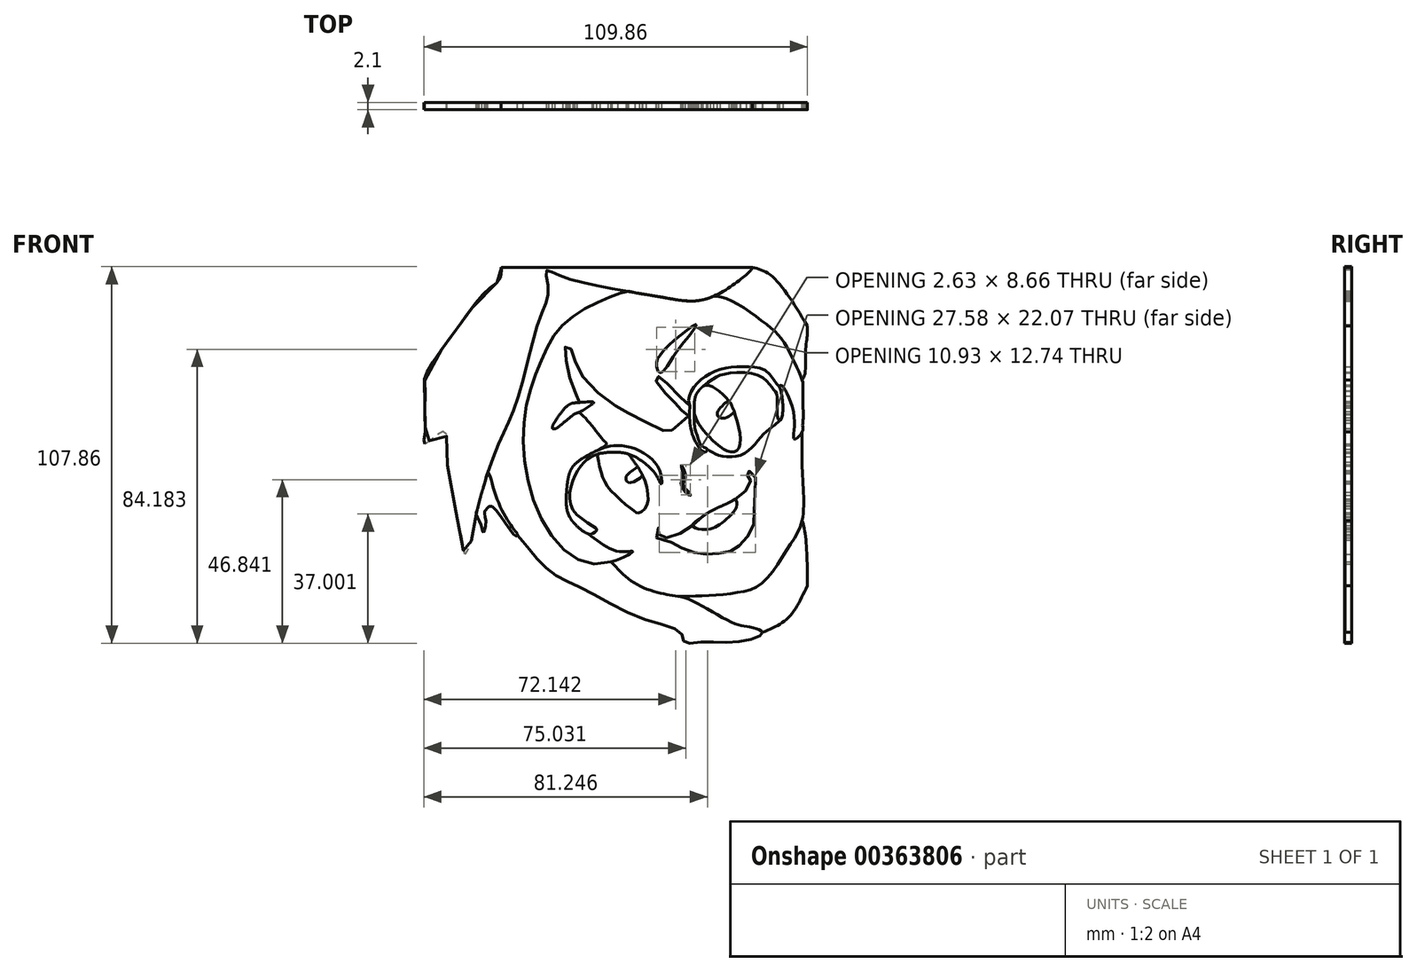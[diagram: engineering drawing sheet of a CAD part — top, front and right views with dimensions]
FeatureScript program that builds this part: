
annotation { "Feature Type Name" : "Feature", "Feature Type Description" : "" }
export const myFeature = defineFeature(function(context is Context, id is Id, definition is map)
    precondition{}
    {
        {
            var Q0;
            Q0=qCreatedBy(makeId("Front.planeOp"),FACE);
            var sketch = newSketch(context, id + "F0", { "sketchPlane" : qUnion([Q0])});
            skFitSpline(sketch, "E0", {"points": [v(-36.35, 49.27) * mm, v(-36.47, 46.64) * mm, v(-40.13, 42.87) * mm, v(-49.67, 30.89) * mm, v(-58.22, 17.8) * mm, v(-58.22, 15.13) * mm, v(-58.22, 10.25) * mm, v(-58.22, 6.14) * mm, v(-58.22, 1.6) * mm, v(-58.22, -1.3) * mm, v(-53.33, 2.26) * mm, v(-52.11, 1.48) * mm, v(-52, -2.07) * mm, v(-50.89, -13.39) * mm, v(-47.45, -29.47) * mm, v(-46.78, -32.91) * mm, v(-45.34, -30.58) * mm, v(-44.23, -25.81) * mm, v(-42.79, -18.49) * mm, v(-37.02, -1.18) * mm, v(-31.92, 10.8) * mm, v(-25.14, 35.1) * mm, v(-22.82, 42.65) * mm, v(-23.37, 48.3) * mm, v(-20.82, 47.42) * mm, v(-8.4, 43.87) * mm, v(11.14, 40.43) * mm, v(24.58, 41) * mm, v(35.66, 49.27) * mm, v(34.22, 49.27) * mm, v(30.33, 49.27) * mm, v(23.45, 49.27) * mm, v(18.46, 49.27) * mm, v(12.25, 49.27) * mm, v(4.7, 49.27) * mm, v(0, 49.27) * mm, v(-3.45, 49.27) * mm, v(-10.94, 49.27) * mm, v(-17.82, 49.27) * mm, v(-22.82, 49.27) * mm, v(-27.03, 49.27) * mm, v(-32.91, 49.27) * mm, v(-35.26, 49.27) * mm, v(-35.59, 49.27) * mm, v(-35.87, 49.27) * mm, v(-36.14, 49.27) * mm, v(-36.24, 49.27) * mm, v(-36.28, 49.27) * mm, v(-36.32, 49.27) * mm, v(-36.35, 49.27) * mm]});
            skFitSpline(sketch, "E1", {"points": [v(0, 42.32) * mm, v(-6.96, 40.03) * mm, v(-18.53, 32.93) * mm, v(-25.14, 21.93) * mm, v(-29.91, 4.2) * mm, v(-25.14, -22.1) * mm, v(-9.38, -35.7) * mm, v(1.33, -32.2) * mm, v(-2.66, -32.16) * mm, v(-11.42, -27.13) * mm, v(-16.81, -22.1) * mm, v(-17.39, -12.6) * mm, v(-14.5, -6.5) * mm, v(-6.32, -1.56) * mm, v(-7.3, 0) * mm, v(-14.12, 7.7) * mm, v(-15.7, 7.06) * mm, v(-18.57, 4.68) * mm, v(-20.93, 2.99) * mm, v(-21.69, 3.17) * mm, v(-20.35, 5.96) * mm, v(-16.1, 10.29) * mm, v(-13.99, 10.54) * mm, v(-15.36, 13.9) * mm, v(-17.69, 22.37) * mm, v(-17.77, 26.74) * mm, v(-16.17, 25.54) * mm, v(-14.25, 19.87) * mm, v(-4.1, 9.84) * mm, v(2.95, 6.12) * mm, v(11.93, 2.04) * mm, v(13.33, 3.63) * mm, v(17.42, 6.39) * mm, v(16.15, 7.51) * mm, v(14.21, 9.68) * mm, v(10.88, 12.89) * mm, v(7.79, 17.54) * mm, v(8.7, 18.03) * mm, v(12.22, 14.88) * mm, v(17.68, 9.62) * mm, v(17.36, 10.85) * mm, v(18.65, 14.62) * mm, v(22.48, 18.17) * mm, v(27.86, 20.38) * mm, v(34.24, 20.73) * mm, v(39.98, 19.22) * mm, v(43.23, 15.2) * mm, v(43.79, 15.48) * mm, v(47.57, 6.47) * mm, v(47.68, 0) * mm, v(49.9, 2.1) * mm, v(50, 3.89) * mm, v(50.14, 5.42) * mm, v(50.14, 9.17) * mm, v(50.14, 13.98) * mm, v(49.88, 16.96) * mm, v(47.5, 22.37) * mm, v(44.07, 28.64) * mm, v(39.45, 33.06) * mm, v(29.56, 39.65) * mm, v(24.58, 41) * mm, v(23.5, 40.55) * mm, v(20.02, 39.7) * mm, v(17.9, 39.58) * mm, v(15.08, 39.79) * mm, v(11.14, 40.43) * mm, v(7.08, 41.12) * mm, v(5.1, 41.45) * mm, v(2.02, 41.97) * mm, v(0, 42.32) * mm]});
            skFitSpline(sketch, "E2", {"points": [v(-40.15, -9.62) * mm, v(-37.89, -16.1) * mm, v(-33.27, -25.08) * mm, v(-31.69, -27.45) * mm, v(-32.35, -27.65) * mm, v(-39.2, -19.14) * mm, v(-40.66, -20.2) * mm, v(-41.19, -20.8) * mm, v(-40.73, -23.96) * mm, v(-41.58, -26.6) * mm, v(-41.98, -24.95) * mm, v(-43.49, -21.53) * mm, v(-43.12, -19.85) * mm, v(-42.79, -18.49) * mm, v(-41.88, -15.18) * mm, v(-40.95, -12.09) * mm, v(-40.15, -9.62) * mm]});
            skFitSpline(sketch, "E3", {"points": [v(-31.69, -27.45) * mm, v(-28.52, -31.21) * mm, v(-22.18, -37.98) * mm, v(-13.33, -42.65) * mm, v(4.58, -51.59) * mm, v(15.23, -55.58) * mm, v(16.16, -58.1) * mm, v(21.39, -58.1) * mm, v(31.18, -58.1) * mm, v(37.8, -56.33) * mm, v(38.55, -55.3) * mm, v(35, -53.81) * mm, v(30.25, -52.7) * mm, v(17.65, -45.97) * mm, v(11.14, -44.48) * mm, v(2.16, -41.4) * mm, v(-4.86, -35.1) * mm], "startDerivative": vector(57.07, -66.54) * mm, "endDerivative": vector(-90.4, 99.22) * mm});
            skFitSpline(sketch, "E4", {"points": [v(15.24, -7.28) * mm, v(15.68, -10.27) * mm, v(15.24, -12.21) * mm, v(16.01, -14.71) * mm, v(17.85, -16.1) * mm, v(17.18, -14.99) * mm, v(15.85, -13.32) * mm, v(16.07, -11.77) * mm, v(16.46, -10.33) * mm, v(15.24, -7.28) * mm]});
            skFitSpline(sketch, "E5", {"points": [v(8.75, -25.3) * mm, v(8.92, -27.43) * mm, v(11.28, -28.17) * mm, v(17.71, -25.34) * mm, v(22.17, -21.54) * mm, v(30.68, -17.22) * mm, v(34.6, -13.5) * mm, v(34.94, -10.8) * mm, v(34, -10.1) * mm, v(34.33, -9.16) * mm, v(36.29, -10.19) * mm, v(36.06, -18.63) * mm, v(35.82, -25.2) * mm, v(32.28, -30.02) * mm, v(29.67, -31.96) * mm, v(25, -32.83) * mm, v(20.05, -32.67) * mm, v(14.95, -30.95) * mm, v(11.34, -29) * mm, v(9.62, -28.9) * mm, v(8.07, -28.06) * mm, v(8.75, -25.3) * mm]});
            skFitSpline(sketch, "E6", {"points": [v(18.46, -24.74) * mm, v(21.5, -25.84) * mm, v(25.1, -25.12) * mm, v(28.43, -22.68) * mm, v(31.1, -19.13) * mm, v(30.68, -17.22) * mm, v(29.68, -17.76) * mm, v(26.52, -19.26) * mm, v(22.78, -21.16) * mm, v(20.99, -22.44) * mm, v(18.46, -24.74) * mm]});
            skFitSpline(sketch, "E7", {"points": [v(-6.02, -2.15) * mm, v(1.24, -2.49) * mm, v(8.68, -8.2) * mm, v(9.57, -12.8) * mm, v(9.18, -12.47) * mm, v(7.85, -9.98) * mm, v(4.96, -7.03) * mm, v(0, -4.2) * mm, v(-7.9, -4.04) * mm, v(-12.01, -6.04) * mm, v(-16, -12.3) * mm, v(-15.18, -21.13) * mm, v(-8.96, -25.95) * mm, v(-10.13, -27) * mm, v(-11.42, -27.13) * mm, v(-16.81, -22.1) * mm, v(-17.63, -15.17) * mm, v(-17.39, -12.6) * mm, v(-16.53, -9.03) * mm, v(-14.5, -6.5) * mm, v(-10.3, -3.94) * mm, v(-6.02, -2.15) * mm]});
            skFitSpline(sketch, "E8", {"points": [v(-8.58, -26.1) * mm, v(-6.34, -26.94) * mm, v(-0.65, -23.86) * mm, v(0.75, -23.76) * mm, v(2.9, -23.39) * mm, v(7.84, -17.51) * mm, v(9.18, -12.47) * mm], "startDerivative": vector(14.15, -11.78) * mm, "endDerivative": vector(3.18, 24.56) * mm});
            skFitSpline(sketch, "E9", {"points": [v(-8.58, -4.2) * mm, v(-7.9, -8.85) * mm, v(-5.03, -14.59) * mm, v(1.47, -20.4) * mm, v(2.89, -21.12) * mm, v(5.4, -18.98) * mm, v(4.3, -10.7) * mm, v(1.43, -6.05) * mm, v(-0.26, -4.13) * mm, v(-2.82, -3.74) * mm, v(-5.66, -3.74) * mm, v(-7.9, -4.04) * mm, v(-8.58, -4.2) * mm]});
            skFitSpline(sketch, "E10", {"points": [v(2.4, -8.06) * mm, v(0.48, -9.57) * mm, v(-0.58, -10.9) * mm, v(0.31, -12.47) * mm, v(4.14, -10.35) * mm, v(3.94, -9.94) * mm, v(3.37, -8.9) * mm, v(2.68, -7.8) * mm, v(2.4, -8.06) * mm]});
            skFitSpline(sketch, "E11", {"points": [v(17.68, 9.62) * mm, v(17.68, 5.06) * mm, v(19.34, -0.78) * mm, v(22.08, -3.69) * mm, v(22.63, -2.82) * mm, v(21.18, -2.04) * mm, v(19.97, 0.51) * mm, v(19.1, 3.34) * mm, v(19.02, 7.3) * mm, v(19.57, 12.9) * mm, v(24.56, 17.34) * mm, v(27.8, 18.7) * mm, v(36.84, 18.54) * mm, v(40.67, 15.54) * mm, v(41.94, 13.99) * mm, v(42.66, 12.82) * mm, v(42.72, 7.05) * mm, v(43.44, 5.39) * mm, v(44.16, 6.61) * mm, v(44, 12.94) * mm, v(43.23, 15.2) * mm], "startDerivative": vector(-4.04, -78.47) * mm, "endDerivative": vector(-20.22, 44.3) * mm});
            skFitSpline(sketch, "E12", {"points": [v(22.63, -2.82) * mm, v(26.24, -4.65) * mm, v(33.12, -4.2) * mm, v(38.4, 1) * mm, v(41.89, 4) * mm, v(43.44, 5.39) * mm], "startDerivative": vector(17.08, -11.47) * mm, "endDerivative": vector(10.5, 10) * mm});
            skFitSpline(sketch, "E13", {"points": [v(19.02, 7.3) * mm, v(20.8, 3.56) * mm, v(25.02, -1) * mm, v(29.68, -3.69) * mm, v(32.01, -1.77) * mm, v(30.57, 7.3) * mm, v(28.4, 11.5) * mm, v(23.8, 15.2) * mm, v(21.52, 15.2) * mm, v(20.25, 13.93) * mm, v(19.33, 12.36) * mm, v(19.02, 7.3) * mm]});
            skFitSpline(sketch, "E14", {"points": [v(28.97, 10.76) * mm, v(26.44, 8.95) * mm, v(25.55, 6.84) * mm, v(27.5, 6.01) * mm, v(30.36, 7.92) * mm, v(30.02, 8.8) * mm, v(28.97, 10.76) * mm]});
            skFitSpline(sketch, "E15", {"points": [v(-13.99, 10.54) * mm, v(-9.84, 10.54) * mm, v(-10.95, 9.62) * mm, v(-14.12, 7.7) * mm, v(-15.7, 7.06) * mm, v(-18.57, 4.68) * mm, v(-20.93, 2.99) * mm, v(-21.69, 3.17) * mm, v(-20.35, 5.96) * mm, v(-17.25, 9.68) * mm, v(-13.99, 10.54) * mm]});
            skFitSpline(sketch, "E16", {"points": [v(9.18, 24.12) * mm, v(8.14, 21.24) * mm, v(9.18, 19.02) * mm, v(12.13, 22.35) * mm, v(15.02, 26.57) * mm, v(19.57, 32.78) * mm, v(15.9, 30.56) * mm, v(9.18, 24.12) * mm]});
            skFitSpline(sketch, "E17", {"points": [v(49.9, 2.1) * mm, v(49.9, -8.83) * mm, v(49.9, -23.25) * mm, v(46.09, -30.69) * mm, v(38.65, -41) * mm, v(30.88, -44) * mm, v(21.18, -44.9) * mm, v(14.21, -44.96) * mm], "startDerivative": vector(-1.96, -68.24) * mm, "endDerivative": vector(-55.6, 0.48) * mm});
            skFitSpline(sketch, "E18", {"points": [v(38.55, -55.3) * mm, v(45.9, -51.12) * mm, v(51.32, -41.98) * mm], "startDerivative": vector(16.84, 6.89) * mm, "endDerivative": vector(8.84, 19.53) * mm});
            skFitSpline(sketch, "E19", {"points": [v(35.66, 49.27) * mm, v(41.05, 46.85) * mm, v(51.32, 32.48) * mm], "startDerivative": vector(14.44, -3.64) * mm, "endDerivative": vector(16.68, -27.77) * mm});
            skFitSpline(sketch, "E20", {"points": [v(51.32, 32.48) * mm, v(51.32, 29.76) * mm, v(50.92, 26.03) * mm, v(50.72, 19.1) * mm, v(49.88, 16.96) * mm], "startDerivative": vector(0.52, -12.72) * mm, "endDerivative": vector(-5.14, -8.7) * mm});
            skFitSpline(sketch, "E21", {"points": [v(49.9, -23.25) * mm, v(50.76, -27.25) * mm, v(51.32, -36.09) * mm, v(51.32, -41.98) * mm], "startDerivative": vector(3.5, -12.8) * mm, "endDerivative": vector(-0.21, -16.49) * mm});
            skSolve(sketch);
        }
        {
            var Q0;
            Q0=makeQuery(id+"F0.imprint","IMPRINT",FACE,{"disambiguationData":[TD([[makeQuery(id+"F0.imprint","IMPRINT",EDGE,{"derivedFrom":sQuery(id+"F0.wireOp",EDGE,"E4")}),-1.0]])]});
            extrude(context, id + "F1", {"entities" : qUnion([Q0]), "depth" : 2 * mm});
        }
        {
            var Q0;
            {var subQ0=sQuery(id+"F0.wireOp",EDGE,"E9");var subQ1=sQuery(id+"F0.wireOp",EDGE,"E7");var subQ8=makeQuery(id+"F0.imprint","INTERSECT",VERTEX,{"disambiguationData":[OD(0.0)],"derivedFrom":[subQ1,subQ0]});Q0=makeQuery(id+"F0.imprint","IMPRINT",FACE,{"disambiguationData":[TD([[makeQuery(id+"F0.imprint","IMPRINT",EDGE,{"disambiguationData":[TD([[subQ8,-1.0]])],"derivedFrom":subQ1}),1.0]])]});}
            var Q1;
            {var subQ0=sQuery(id+"F0.wireOp",EDGE,"E13");var subQ1=sQuery(id+"F0.wireOp",EDGE,"E11");var subQ2=makeQuery(id+"F0.imprint","INTERSECT",VERTEX,{"disambiguationData":[OD(0.0)],"derivedFrom":[subQ1,subQ0]});Q1=makeQuery(id+"F0.imprint","IMPRINT",FACE,{"disambiguationData":[TD([[makeQuery(id+"F0.imprint","IMPRINT",EDGE,{"disambiguationData":[TD([[subQ2,-1.0]])],"derivedFrom":subQ1}),-1.0]])]});}
            extrude(context, id + "F2", {"entities" : qUnion([Q0, Q1]), "operationType" : NewBodyOperationType.ADD, "depth" : 2.1 * mm});
        }
        {
            var Q0;
            {var subQ6=sQuery(id+"F0.wireOp",EDGE,"E12");Q0=makeQuery(id+"F0.imprint","IMPRINT",FACE,{"disambiguationData":[TD([[makeQuery(id+"F0.imprint","IMPRINT",EDGE,{"derivedFrom":subQ6}),1.0]])]});}
            extrude(context, id + "F3", {"entities" : qUnion([Q0]), "depth" : 2 * mm});
        }
        {
            var Q0;
            Q0=makeQuery(id+"F0.imprint","IMPRINT",FACE,{"disambiguationData":[TD([[makeQuery(id+"F0.imprint","IMPRINT",EDGE,{"derivedFrom":sQuery(id+"F0.wireOp",EDGE,"E16")}),-1.0]])]});
            extrude(context, id + "F4", {"entities" : qUnion([Q0]), "operationType" : NewBodyOperationType.ADD, "depth" : 2.1 * mm});
        }
        {
            var Q0;
            {var subQ0=sQuery(id+"F0.wireOp",EDGE,"E3");var subQ9=makeQuery(id+"F0.imprint","IMPRINT",VERTEX,{"derivedFrom":subQ0});Q0=makeQuery(id+"F0.imprint","IMPRINT",FACE,{"disambiguationData":[TD([[makeQuery(id+"F0.imprint","IMPRINT",EDGE,{"disambiguationData":[TD([[subQ9,1.0]])],"derivedFrom":subQ0}),1.0]])]});}
            var Q1;
            {var subQ0=sQuery(id+"F0.wireOp",EDGE,"E19");Q1=makeQuery(id+"F0.imprint","IMPRINT",FACE,{"disambiguationData":[TD([[makeQuery(id+"F0.imprint","IMPRINT",EDGE,{"derivedFrom":subQ0}),-1.0]])]});}
            extrude(context, id + "F5", {"entities" : qUnion([Q0, Q1]), "depth" : 2.1 * mm});
        }
        {
            var Q0;
            {var subQ0=sQuery(id+"F0.wireOp",EDGE,"E2");var subQ2=sQuery(id+"F0.wireOp",EDGE,"E0");var subQ8=makeQuery(id+"F0.imprint","INTERSECT",VERTEX,{"disambiguationData":[OD(0.0)],"derivedFrom":[subQ2,subQ0]});Q0=makeQuery(id+"F0.imprint","IMPRINT",FACE,{"disambiguationData":[TD([[makeQuery(id+"F0.imprint","IMPRINT",EDGE,{"disambiguationData":[TD([[subQ8,-1.0]])],"derivedFrom":subQ2}),-1.0]])]});}
            extrude(context, id + "F6", {"entities" : qUnion([Q0]), "operationType" : NewBodyOperationType.ADD, "depth" : 2.1 * mm});
        }
        {
            var Q0;
            {var subQ0=sQuery(id+"F0.wireOp",EDGE,"E0");var subQ2=sQuery(id+"F0.wireOp",EDGE,"E2");var subQ7=makeQuery(id+"F0.imprint","INTERSECT",VERTEX,{"disambiguationData":[OD(1.0)],"derivedFrom":[subQ0,subQ2]});Q0=makeQuery(id+"F0.imprint","IMPRINT",FACE,{"disambiguationData":[TD([[makeQuery(id+"F0.imprint","IMPRINT",EDGE,{"disambiguationData":[TD([[subQ7,-1.0]])],"derivedFrom":subQ0}),1.0]])]});}
            extrude(context, id + "F7", {"entities" : qUnion([Q0]), "depth" : 2.1 * mm});
        }
        {
            var Q0;
            {var subQ3=sQuery(id+"F0.wireOp",EDGE,"E18");Q0=makeQuery(id+"F0.imprint","IMPRINT",FACE,{"disambiguationData":[TD([[makeQuery(id+"F0.imprint","IMPRINT",EDGE,{"derivedFrom":subQ3}),1.0]])]});}
            extrude(context, id + "F8", {"entities" : qUnion([Q0]), "operationType" : NewBodyOperationType.ADD, "depth" : 1.9 * mm});
        }
        {
            var Q0;
            {var subQ0=sQuery(id+"F0.wireOp",EDGE,"E6");var subQ1=sQuery(id+"F0.wireOp",EDGE,"E5");var subQ7=makeQuery(id+"F0.imprint","INTERSECT",VERTEX,{"disambiguationData":[OD(0.0)],"derivedFrom":[subQ1,subQ0]});Q0=makeQuery(id+"F0.imprint","IMPRINT",FACE,{"disambiguationData":[TD([[makeQuery(id+"F0.imprint","IMPRINT",EDGE,{"disambiguationData":[TD([[subQ7,1.0]])],"derivedFrom":subQ1}),-1.0]])]});}
            extrude(context, id + "F9", {"entities" : qUnion([Q0]), "operationType" : NewBodyOperationType.ADD, "depth" : 2.1 * mm});
        }
        {
            var Q0;
            {var subQ1=sQuery(id+"F0.wireOp",EDGE,"E2");var subQ4=sQuery(id+"F0.wireOp",EDGE,"E0");var subQ5=makeQuery(id+"F0.imprint","INTERSECT",VERTEX,{"disambiguationData":[OD(5.0)],"derivedFrom":[subQ4,subQ1]});Q0=makeQuery(id+"F0.imprint","IMPRINT",FACE,{"disambiguationData":[TD([[makeQuery(id+"F0.imprint","IMPRINT",EDGE,{"disambiguationData":[TD([[subQ5,-1.0]])],"derivedFrom":subQ4}),-1.0]])]});}
            extrude(context, id + "F10", {"entities" : qUnion([Q0]), "depth" : 2.1 * mm});
        }
    });
